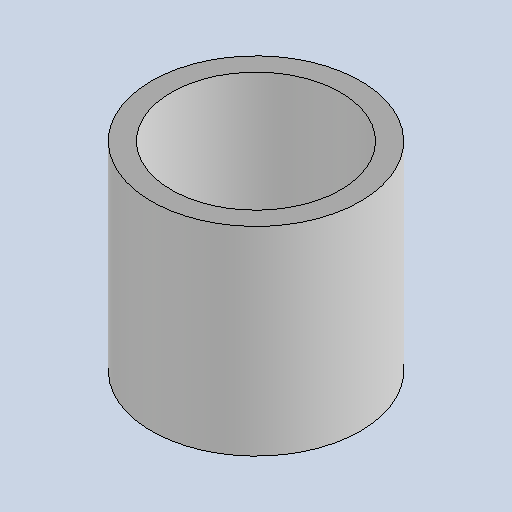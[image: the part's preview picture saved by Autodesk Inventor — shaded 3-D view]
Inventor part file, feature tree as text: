
AUTODESK INVENTOR PART (.ipt)
format: ipt  version: 2025.1 (Build 291241020, 241B)  size: 126,464 bytes
history: native  units: mm
features: extrude x1, sketch x1
ambient origin geometry x8: Origin, YZ Plane, XZ Plane, XY Plane, X Axis, Y Axis, Z Axis, Center Point
bodies: Body1 (feature_tree)
feature tree (2):
  extrude  "Extrusion5"  Depth=20.0mm
  sketch  "Sketch11"  dims[d187=21.0mm d188=2.0mm d189=20.0mm d190=0.0mm]
